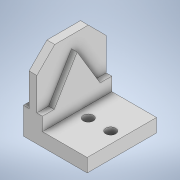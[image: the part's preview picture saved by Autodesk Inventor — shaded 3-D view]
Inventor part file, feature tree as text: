
AUTODESK INVENTOR PART (.ipt)
format: ipt  version: 2022 (Build 260153000, 153)  size: 186,368 bytes
history: native  units: in
note: dims shown in document units (in); Inventor stores cm internally (conversion verified against a paired STEP export)
features: sketch x6, extrude x5, mirror x3, other x3, projected_geometry x2, chamfer x1
ambient origin geometry x8: Origin, YZ Plane, XZ Plane, XY Plane, X Axis, Y Axis, Z Axis, Center Point
bodies: Solid1 (feature_tree)
feature tree (20):
  extrude  "Extrusion1"  Depth=0.8858in
  extrude  "Extrusion4"  Depth=0.1378in
  mirror  "Mirror2"
  extrude  "Extrusion5"  Depth=0.0984in TaperAngle=0.0deg
  extrude  "Extrusion6"  Depth=0.3937in TaperAngle=0.0deg
  mirror  "Mirror3"
  mirror  "Mirror4"
  sketch  "Sketch9"  dims[d40=0.1575in]
  other  "Work Point4"
  other  "Work Point5"
  other  "Work Point6"
  chamfer  "Chamfer1"  Distance=0.315in Angle=45.0deg
  extrude  "Extrusion7"  Depth=0.7874in
  sketch  "Sketch1"  dims[d0=1.2205in d1=0.8858in]
  sketch  "Sketch2"  dims[d2=0.1378in d3=0.0in d31=0.8067in]
  sketch  "Sketch7"  dims[d33=0.6723in d34=0.0984in d35=0.0in]
  projected_geometry  "Projected Loop2"
  sketch  "Sketch8"  dims[d36=0.4724in d37=0.0in d38=0.3937in d39=0.0in]
  projected_geometry  "Projected Loop3"
  sketch  "Sketch10"  dims[d50=0.3937in d60=0.315in d61=0.0787in d62=45.0deg d63=0.7874in d64=0.1772in d65=0.3937in d66=0.2362in d67=0.0in d68=0.0344in d69=0.0197in d70=0.0344in]
